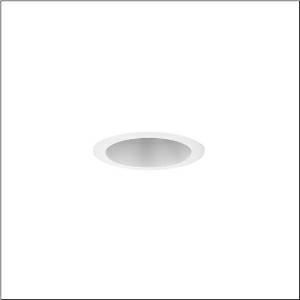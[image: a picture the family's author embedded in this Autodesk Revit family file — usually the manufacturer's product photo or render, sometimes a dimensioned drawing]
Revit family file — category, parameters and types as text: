
# Revit family: lunis_31-l_51dn16me31b
name_source: partatom
category: Lighting Fixtures
units: mm (PartAtom-declared; Revit-internal decimal feet)

## family parameters
Cut with Voids When Loaded = No
Host = Face
Light Source = No
Part Type = Normal
Room Calculation Point = No
Round Connector Dimension = Use Diameter
Shared = No

## types (1)
- --- (1 x LED, 1600 lm, 11.5 W, 3000K)
    Apparent Load = 12 VA
    CIE Flux Codes = 76 93 99 100 100
    Color Rendering = 80
    Color Temperature = 3000K
    Default Elevation = 1800 mm
    Description = Lunis 31, -L, downlight, light control with reflector, light emission: direct distribution, LED rated luminous flux: 1.600lm, light colour: 830, mains connection: 220..240V, AC/DC, 0/50..60Hz, housing, of aluminium, white, protection rating (complete): IP20, protection rating (on room side): IP54, insulation class (complete): insulation class II (safety insulation), certification: CE, ENEC, packaging unit: 1 piece
    Height = 0 mm  [stored 0 ft]
    Lamp = 1 x LED
    Lamp Light Flux = 1600 lm
    Lamp Power = 11.5 W
    Lamp count = 1
    Length = 188 mm  [stored 0.616798 ft]
    Luminous efficacy = 139 lm/W
    Manufacturer = Siteco
    ModVariant = No
    Model = 51DN16ME31B
    Mounting Place = Ceiling
    Mounting Type = Recessed
    Number of Poles = 1
    OnlyDefault = Yes
    Power Factor = 1
    Product Name = Lunis 31-L
    Product group = downlight
    ProductGroupID = 401
    Protection Class = Protection class II
    Protection Degree = IP 20
    RLX_Detail_Level = 1
    RLX_Emergency_Light_Flux = 0 lm
    RLX_Emergency_Type = 0
    RLX_Emergency_Type_DB = No
    RlxData = <blob elided: 22497 chars, md5=9fe744a7>
    Socket = socket
    Standby Power = 0 W
    System Light Flux = 1600 lm
    System Power = 12 W
    Type Comments = individual setting: luminous flux: 100 % | (OFF | ON) | 300 mA
    Type Image = l_1345911.jpg
    URL = http://relux.com
    VarID = @adj_029981
    Voltage = 0 V
    Weight = 0.00 kg
    Width = 0 mm  [stored 0 ft]

note: [stored X ft] marks values corroborated as IEEE doubles in the binary element streams (Revit-internal decimal feet)

## geometry (parser evidence)
native form markers: Blend x4, Sweep x12
no freeform markers — native parametric forms only
